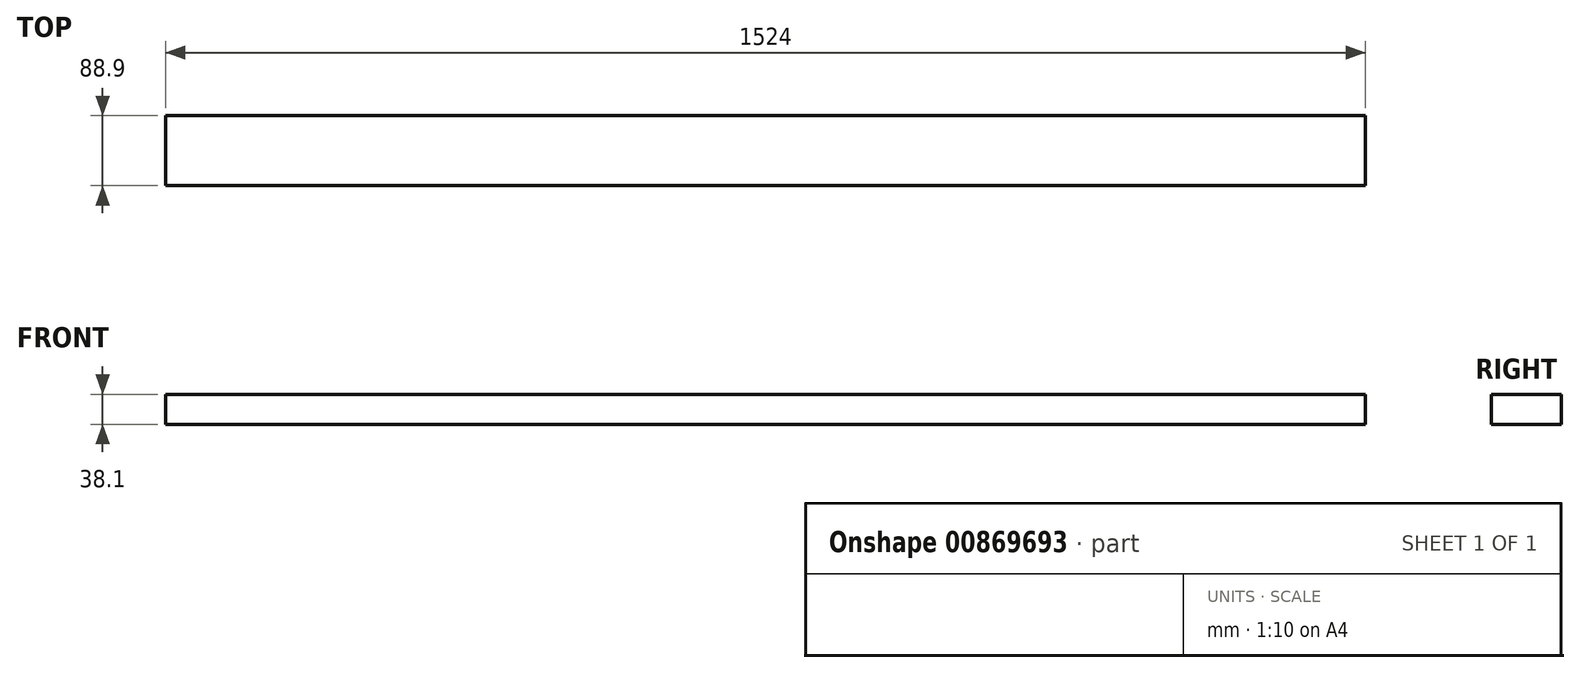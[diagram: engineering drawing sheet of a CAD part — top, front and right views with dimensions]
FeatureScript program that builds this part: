
annotation { "Feature Type Name" : "Feature", "Feature Type Description" : "" }
export const myFeature = defineFeature(function(context is Context, id is Id, definition is map)
    precondition{}
    {
        {
            var Q0;
            Q0=qCreatedBy(makeId("Top.planeOp"),FACE);
            var sketch = newSketch(context, id + "F0", { "sketchPlane" : qUnion([Q0])});
            skLineSegment(sketch, "E0.bottom", {"start": v(0, 0) * mm, "end": v(1524, 0) * mm});
            skLineSegment(sketch, "E0.top", {"start": v(0, -88.9) * mm, "end": v(1524, -88.9) * mm});
            skLineSegment(sketch, "E0.left", {"start": v(0, 0) * mm, "end": v(0, -88.9) * mm});
            skLineSegment(sketch, "E0.right", {"start": v(1524, 0) * mm, "end": v(1524, -88.9) * mm});
            skSolve(sketch);
        }
        {
            var Q0;
            Q0 = qSketchRegion(id + "F0", true);
            extrude(context, id + "F1", {"entities" : qUnion([Q0]), "depth" : 38.1 * mm, "offsetDistance" : 25.4 * mm});
        }
    });
